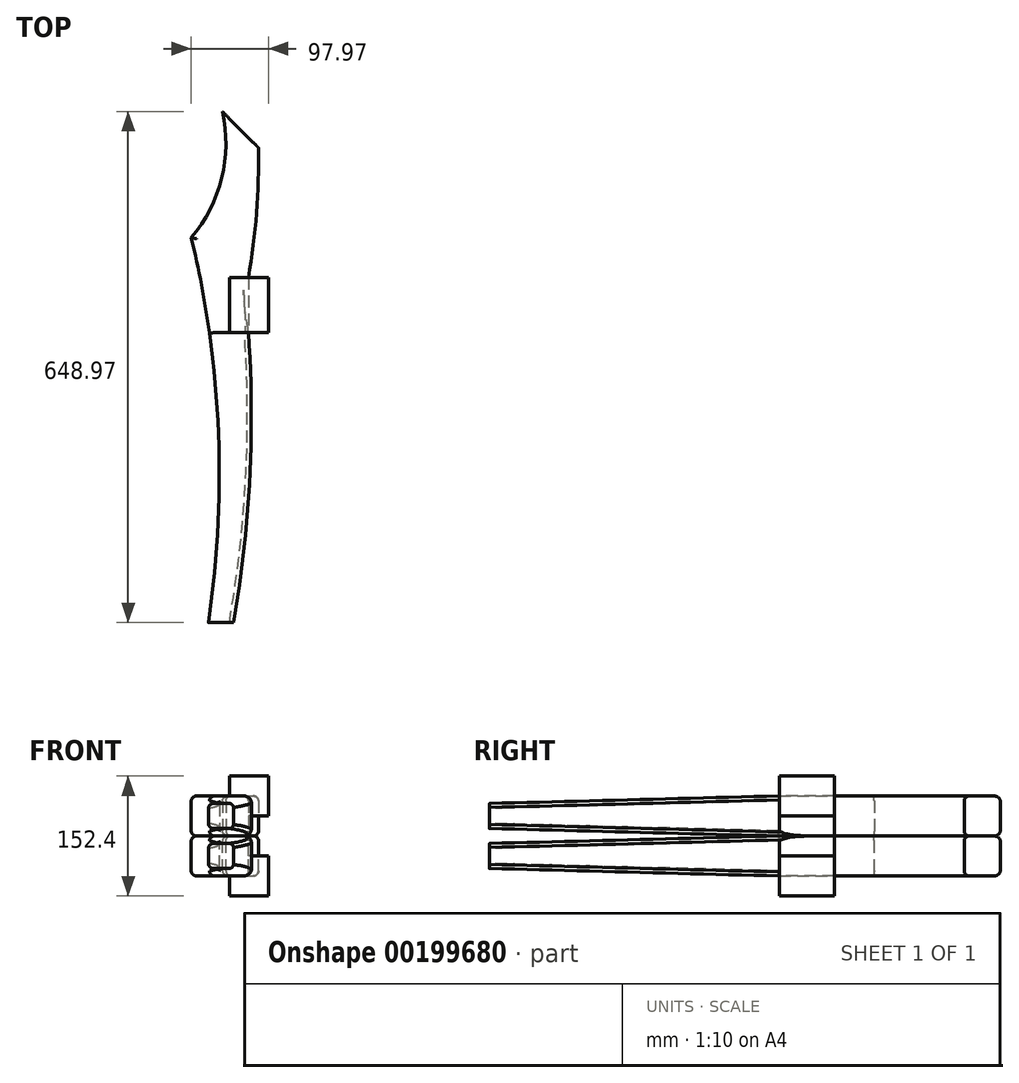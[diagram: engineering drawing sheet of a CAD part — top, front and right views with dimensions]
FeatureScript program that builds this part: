
annotation { "Feature Type Name" : "Feature", "Feature Type Description" : "" }
export const myFeature = defineFeature(function(context is Context, id is Id, definition is map)
    precondition{}
    {
        {
            var Q0;
            Q0=qCreatedBy(makeId("Top.planeOp"),FACE);
            var sketch = newSketch(context, id + "F0", { "sketchPlane" : qUnion([Q0])});
            skLineSegment(sketch, "E0", {"start": v(0, 0) * mm, "end": v(0, -69.85) * mm});
            skArc(sketch, "E1", {"start": v(0, 0) * mm, "mid": v(10.36, 82.24) * mm, "end": v(12.7, 165.1) * mm});
            skArc(sketch, "E2", {"start": v(-19.05, -438.15) * mm, "mid": v(1.7, -254.58) * mm, "end": v(0, -69.85) * mm});
            skLineSegment(sketch, "E3", {"start": v(-19.05, -438.15) * mm, "end": v(-50.8, -438.15) * mm});
            skArc(sketch, "E4", {"start": v(-50.8, -438.15) * mm, "mid": v(-38.16, -192.63) * mm, "end": v(-72.57, 50.8) * mm});
            skArc(sketch, "E5", {"start": v(-72.57, 50.8) * mm, "mid": v(-33.92, 126.15) * mm, "end": v(-33.02, 210.82) * mm});
            skLineSegment(sketch, "E6", {"start": v(-33.02, 210.82) * mm, "end": v(12.7, 165.1) * mm});
            skLineSegment(sketch, "E7", {"start": v(12.7, 165.1) * mm, "end": v(12.7, 334.3) * mm, "construction": true});
            skSolve(sketch);
        }
        {
            var Q0;
            Q0=makeQuery(id+"F0.imprint","IMPRINT",FACE,{"disambiguationData":[TD([[makeQuery(id+"F0.imprint","IMPRINT",EDGE,{"derivedFrom":sQuery(id+"F0.wireOp",EDGE,"E0")}),-1.0]])]});
            extrude(context, id + "F1", {"entities" : qUnion([Q0]), "depth" : 50.8 * mm});
        }
        {
            var Q0;
            Q0=makeQuery(id+"F1.opExtrude","SWEPT_FACE",FACE,{"disambiguationData":[OSD([sQuery(id+"F0.wireOp",EDGE,"E0")])]});
            var sketch = newSketch(context, id + "F2", { "sketchPlane" : qUnion([Q0])});
            skLineSegment(sketch, "E8.bottom", {"start": v(0, 25.4) * mm, "end": v(-69.85, 25.4) * mm});
            skLineSegment(sketch, "E8.top", {"start": v(0, 50.8) * mm, "end": v(-69.85, 50.8) * mm});
            skLineSegment(sketch, "E8.left", {"start": v(0, 25.4) * mm, "end": v(0, 50.8) * mm});
            skLineSegment(sketch, "E8.right", {"start": v(-69.85, 25.4) * mm, "end": v(-69.85, 50.8) * mm});
            skSolve(sketch);
        }
        {
            var Q0;
            Q0=makeQuery(id+"F2.imprint","IMPRINT",FACE,{"disambiguationData":[TD([[makeQuery(id+"F2.imprint","IMPRINT",EDGE,{"derivedFrom":sQuery(id+"F2.wireOp",EDGE,"E8.bottom")}),-1.0]])]});
            extrude(context, id + "F3", {"entities" : qUnion([Q0]), "operationType" : NewBodyOperationType.ADD, "depth" : 25.4 * mm});
        }
        {
            var Q0;
            Q0=makeQuery(id+"F3.boolean.opBoolean","MERGE",FACE,{"derivedFrom":[makeQuery(id+"F1.opExtrude","CAP_FACE",FACE,{"disambiguationData":[OSD([sQuery(id+"F0.wireOp",EDGE,"E0"),sQuery(id+"F0.wireOp",EDGE,"E1"),sQuery(id+"F0.wireOp",EDGE,"E2"),sQuery(id+"F0.wireOp",EDGE,"E3"),sQuery(id+"F0.wireOp",EDGE,"E4"),sQuery(id+"F0.wireOp",EDGE,"E5"),sQuery(id+"F0.wireOp",EDGE,"E6")])],"isStart":false}),makeQuery(id+"F3.opExtrude","SWEPT_FACE",FACE,{"disambiguationData":[OSD([sQuery(id+"F2.wireOp",EDGE,"E8.top")])]})]});
            var sketch = newSketch(context, id + "F4", { "sketchPlane" : qUnion([Q0])});
            skLineSegment(sketch, "E9.bottom", {"start": v(25.4, 0) * mm, "end": v(-23.9, 0) * mm});
            skLineSegment(sketch, "E9.top", {"start": v(25.4, -69.85) * mm, "end": v(-23.9, -69.85) * mm});
            skLineSegment(sketch, "E9.left", {"start": v(25.4, 0) * mm, "end": v(25.4, -69.85) * mm});
            skLineSegment(sketch, "E9.right", {"start": v(-23.9, 0) * mm, "end": v(-23.9, -69.85) * mm});
            skSolve(sketch);
        }
        {
            var Q0;
            {var subQ0=sQuery(id+"F4.wireOp",EDGE,"E9.left");Q0=makeQuery(id+"F4.imprint","IMPRINT",FACE,{"disambiguationData":[TD([[makeQuery(id+"F4.imprint","IMPRINT",EDGE,{"derivedFrom":subQ0}),-1.0]])]});}
            extrude(context, id + "F5", {"entities" : qUnion([Q0]), "operationType" : NewBodyOperationType.ADD, "depth" : 25.4 * mm});
        }
        {
            var Q0;
            Q0=qCreatedBy(makeId("Right.planeOp"),FACE);
            cPlane(context, id + "F6", {"entities" : qUnion([Q0]), "cplaneType" : CPlaneType.OFFSET, "offset" : 76.2 * mm, "oppositeDirection" : true, "width" : 152.4 * mm, "height" : 152.4 * mm});
        }
        {
            var Q0;
            Q0=qCreatedBy(id+"F6.planeOp",FACE);
            var sketch = newSketch(context, id + "F7", { "sketchPlane" : qUnion([Q0])});
            skLineSegment(sketch, "E10", {"start": v(-438.15, 9.52) * mm, "end": v(-69.85, 0) * mm});
            skLineSegment(sketch, "E11", {"start": v(-438.15, 41.27) * mm, "end": v(-69.85, 50.8) * mm});
            skLineSegment(sketch, "E12", {"start": v(-69.85, 0) * mm, "end": v(-438.15, 0) * mm});
            skLineSegment(sketch, "E13", {"start": v(-438.15, 0) * mm, "end": v(-438.15, 9.52) * mm});
            skLineSegment(sketch, "E14", {"start": v(-438.15, 50.8) * mm, "end": v(-69.85, 50.8) * mm});
            skLineSegment(sketch, "E15.trimOffspring", {"start": v(-438.15, 41.27) * mm, "end": v(-438.15, 50.8) * mm});
            skSolve(sketch);
        }
        {
            var Q0;
            Q0=makeQuery(id+"F7.imprint","IMPRINT",FACE,{"disambiguationData":[TD([[makeQuery(id+"F7.imprint","IMPRINT",EDGE,{"derivedFrom":sQuery(id+"F7.wireOp",EDGE,"E10")}),-1.0]])]});
            var Q1;
            Q1=makeQuery(id+"F7.imprint","IMPRINT",FACE,{"disambiguationData":[TD([[makeQuery(id+"F7.imprint","IMPRINT",EDGE,{"derivedFrom":sQuery(id+"F7.wireOp",EDGE,"E11")}),1.0]])]});
            extrude(context, id + "F8", {"entities" : qUnion([Q0, Q1]), "operationType" : NewBodyOperationType.REMOVE, "depth" : 152.4 * mm});
        }
        {
            var Q0;
            Q0=makeQuery(id+"F8.boolean.opBoolean","INTERSECT",EDGE,{"derivedFrom":[makeQuery(id+"F1.opExtrude","SWEPT_FACE",FACE,{"disambiguationData":[OSD([sQuery(id+"F0.wireOp",EDGE,"E4")])]}),makeQuery(id+"F8.opExtrude","SWEPT_FACE",FACE,{"disambiguationData":[OSD([sQuery(id+"F7.wireOp",EDGE,"E11")])]})]});
            var Q1;
            Q1=makeQuery(id+"F1.opExtrude","CAP_EDGE",EDGE,{"disambiguationData":[OSD([sQuery(id+"F0.wireOp",EDGE,"E4")])],"isStart":false});
            var Q2;
            Q2=makeQuery(id+"F1.opExtrude","CAP_EDGE",EDGE,{"disambiguationData":[OSD([sQuery(id+"F0.wireOp",EDGE,"E5")])],"isStart":false});
            var Q3;
            Q3=makeQuery(id+"F1.opExtrude","CAP_EDGE",EDGE,{"disambiguationData":[OSD([sQuery(id+"F0.wireOp",EDGE,"E1")])],"isStart":false});
            var Q4;
            Q4=makeQuery(id+"F1.opExtrude","CAP_EDGE",EDGE,{"disambiguationData":[OSD([sQuery(id+"F0.wireOp",EDGE,"E5")])],"isStart":true});
            var Q5;
            Q5=makeQuery(id+"F1.opExtrude","CAP_EDGE",EDGE,{"disambiguationData":[OSD([sQuery(id+"F0.wireOp",EDGE,"E4")])],"isStart":true});
            var Q6;
            Q6=makeQuery(id+"F8.boolean.opBoolean","INTERSECT",EDGE,{"derivedFrom":[makeQuery(id+"F1.opExtrude","SWEPT_FACE",FACE,{"disambiguationData":[OSD([sQuery(id+"F0.wireOp",EDGE,"E4")])]}),makeQuery(id+"F8.opExtrude","SWEPT_FACE",FACE,{"disambiguationData":[OSD([sQuery(id+"F7.wireOp",EDGE,"E10")])]})]});
            var Q7;
            Q7=makeQuery(id+"F1.opExtrude","CAP_EDGE",EDGE,{"disambiguationData":[OSD([sQuery(id+"F0.wireOp",EDGE,"E1")])],"isStart":true});
            var Q8;
            Q8=makeQuery(id+"F1.opExtrude","CAP_EDGE",EDGE,{"disambiguationData":[OSD([sQuery(id+"F0.wireOp",EDGE,"E0")])],"isStart":true});
            var Q9;
            Q9=makeQuery(id+"F1.opExtrude","CAP_EDGE",EDGE,{"disambiguationData":[OSD([sQuery(id+"F0.wireOp",EDGE,"E0")])],"isStart":false});
            fillet(context, id + "F9", {"entities" : qUnion([Q0, Q1, Q2, Q3, Q4, Q5, Q6, Q7, Q8, Q9]), "radius" : 6.35 * mm, "allowEdgeOverflow" : false});
        }
        {
            var Q0;
            Q0=makeQuery(id+"F8.boolean.opBoolean","INTERSECT",EDGE,{"derivedFrom":[makeQuery(id+"F1.opExtrude","SWEPT_FACE",FACE,{"disambiguationData":[OSD([sQuery(id+"F0.wireOp",EDGE,"E2")])]}),makeQuery(id+"F8.opExtrude","SWEPT_FACE",FACE,{"disambiguationData":[OSD([sQuery(id+"F7.wireOp",EDGE,"E10")])]})]});
            var Q1;
            Q1=makeQuery(id+"F8.boolean.opBoolean","INTERSECT",EDGE,{"derivedFrom":[makeQuery(id+"F1.opExtrude","SWEPT_FACE",FACE,{"disambiguationData":[OSD([sQuery(id+"F0.wireOp",EDGE,"E2")])]}),makeQuery(id+"F8.opExtrude","SWEPT_FACE",FACE,{"disambiguationData":[OSD([sQuery(id+"F7.wireOp",EDGE,"E11")])]})]});
            fillet(context, id + "F10", {"entities" : qUnion([Q0, Q1]), "radius" : 5.08 * mm, "tangentPropagation" : true, "allowEdgeOverflow" : false});
        }
        {
            var Q0;
            Q0=makeQuery(id+"F1.opExtrude","SWEPT_BODY",BODY,{"disambiguationData":[OSD([sQuery(id+"F0.wireOp",EDGE,"E0"),sQuery(id+"F0.wireOp",EDGE,"E1"),sQuery(id+"F0.wireOp",EDGE,"E2"),sQuery(id+"F0.wireOp",EDGE,"E3"),sQuery(id+"F0.wireOp",EDGE,"E4"),sQuery(id+"F0.wireOp",EDGE,"E5"),sQuery(id+"F0.wireOp",EDGE,"E6")])]});
            var Q1;
            Q1=makeQuery(id+"F0.imprint","IMPRINT",FACE,{"disambiguationData":[TD([[makeQuery(id+"F0.imprint","IMPRINT",EDGE,{"derivedFrom":sQuery(id+"F0.wireOp",EDGE,"E0")}),-1.0]])]});
            mirror(context, id + "F11", {"entities" : qUnion([Q0]), "mirrorPlane" : qUnion([Q1])});
        }
    });
